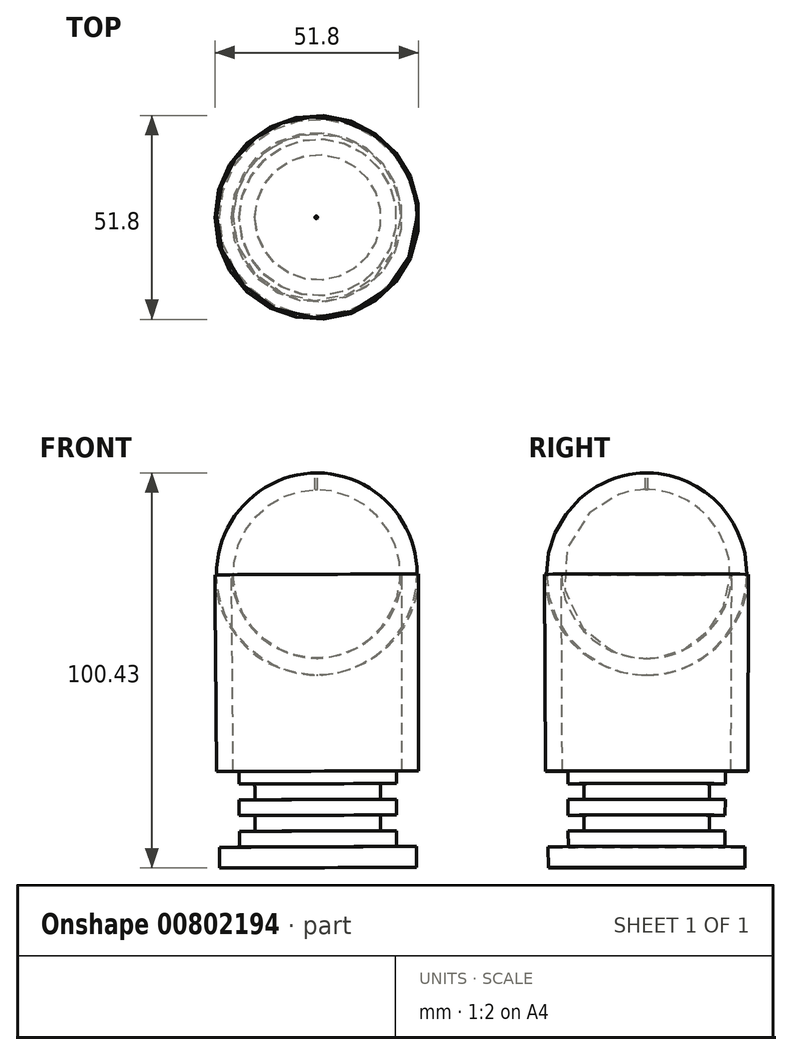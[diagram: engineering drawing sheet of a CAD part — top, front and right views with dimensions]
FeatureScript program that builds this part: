
annotation { "Feature Type Name" : "Feature", "Feature Type Description" : "" }
export const myFeature = defineFeature(function(context is Context, id is Id, definition is map)
    precondition{}
    {
        {
            var Q0;
            Q0=qCreatedBy(makeId("Front.planeOp"),FACE);
            var sketch = newSketch(context, id + "F0", { "sketchPlane" : qUnion([Q0])});
            skLineSegment(sketch, "E0", {"start": v(0, 7.24) * mm, "end": v(20, 7.24) * mm});
            skLineSegment(sketch, "E1", {"start": v(20, 7.24) * mm, "end": v(20, 4) * mm});
            skLineSegment(sketch, "E2", {"start": v(20, 4) * mm, "end": v(16, 4) * mm});
            skLineSegment(sketch, "E3", {"start": v(16, 4) * mm, "end": v(16, 0) * mm});
            skLineSegment(sketch, "E4", {"start": v(16, 0) * mm, "end": v(20, 0) * mm});
            skLineSegment(sketch, "E5", {"start": v(20, 0) * mm, "end": v(20, -4) * mm});
            skLineSegment(sketch, "E6", {"start": v(20, -4) * mm, "end": v(16, -4) * mm});
            skLineSegment(sketch, "E7", {"start": v(16, -4) * mm, "end": v(16, -8) * mm});
            skLineSegment(sketch, "E8", {"start": v(16, -8) * mm, "end": v(20, -8) * mm});
            skLineSegment(sketch, "E9", {"start": v(20, -8) * mm, "end": v(20, -12) * mm});
            skLineSegment(sketch, "E10", {"start": v(20, -12) * mm, "end": v(25.1, -12) * mm});
            skLineSegment(sketch, "E11", {"start": v(25.1, -12) * mm, "end": v(25.1, -17.29) * mm});
            skLineSegment(sketch, "E12", {"start": v(25.1, -17.29) * mm, "end": v(0.1, -17.29) * mm});
            skLineSegment(sketch, "E13", {"start": v(0.1, -17.29) * mm, "end": v(0, 7.24) * mm});
            skLineSegment(sketch, "E14", {"start": v(21.43, 7.24) * mm, "end": v(21.43, 57.24) * mm});
            skArc(sketch, "E15", {"start": v(21.43, 57.24) * mm, "mid": v(15.15, 72.4) * mm, "end": v(0, 78.67) * mm});
            skArc(sketch, "E16.0", {"start": v(25.69, 57.24) * mm, "mid": v(18.16, 75.4) * mm, "end": v(0, 82.93) * mm});
            skLineSegment(sketch, "E16.1", {"start": v(25.69, 7.24) * mm, "end": v(25.69, 57.24) * mm});
            skLineSegment(sketch, "E17", {"start": v(25.69, 7.24) * mm, "end": v(21.43, 7.24) * mm});
            skLineSegment(sketch, "E18", {"start": v(0, 78.67) * mm, "end": v(0, 82.93) * mm});
            skSolve(sketch);
        }
        {
            var Q0;
            Q0 = qSketchRegion(id + "F0", true);
            var Q1;
            Q1=sQuery(id+"F0.wireOp",EDGE,"E13");
            revolve(context, id + "F1", {"surfaceOperationType" : NewSurfaceOperationType.NEW, "entities" : qUnion([Q0]), "axis" : qUnion([Q1]), "revolveType" : RevolveType.FULL});
        }
    });
